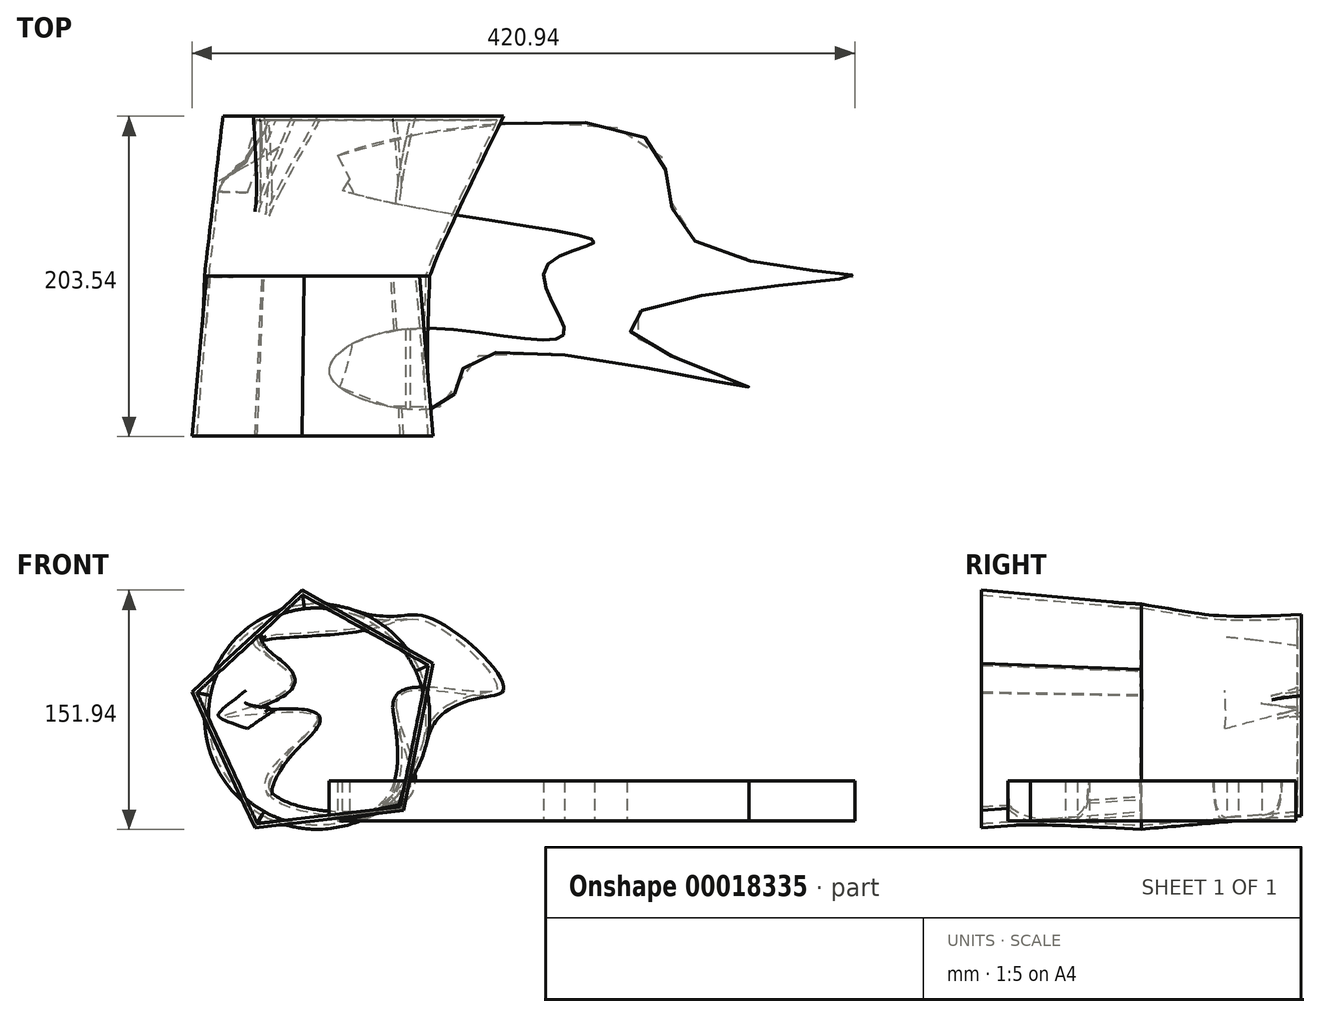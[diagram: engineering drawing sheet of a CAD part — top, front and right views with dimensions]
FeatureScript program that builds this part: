
annotation { "Feature Type Name" : "Feature", "Feature Type Description" : "" }
export const myFeature = defineFeature(function(context is Context, id is Id, definition is map)
    precondition{}
    {
        {
            var Q0;
            Q0=qCreatedBy(makeId("Front.planeOp"),FACE);
            var sketch = newSketch(context, id + "F0", { "sketchPlane" : qUnion([Q0])});
            skFitSpline(sketch, "E0", {"points": [v(0, 0) * mm, v(-33.29, -44.54) * mm, v(59.25, -50.49) * mm, v(52.28, 13.37) * mm, v(117.29, 15.44) * mm, v(73.43, 62.05) * mm, v(28.41, 56.64) * mm, v(-40.52, 46.45) * mm, v(-15.95, 21.27) * mm, v(-59.81, 0) * mm, v(0, 0) * mm]});
            skSolve(sketch);
        }
        {
            var Q0;
            Q0=makeQuery(id+"F0.imprint","IMPRINT",FACE,{"disambiguationData":[TD([[makeQuery(id+"F0.imprint","IMPRINT",EDGE,{"derivedFrom":sQuery(id+"F0.wireOp",EDGE,"E0")}),1.0]])]});
            cPlane(context, id + "F1", {"entities" : qUnion([Q0]), "cplaneType" : CPlaneType.OFFSET, "offset" : 101.6 * mm, "width" : 152.4 * mm, "height" : 152.4 * mm});
        }
        {
            var Q0;
            Q0=qCreatedBy(id+"F1.planeOp",FACE);
            var sketch = newSketch(context, id + "F2", { "sketchPlane" : qUnion([Q0])});
            skPoint(sketch, "E1.0", {"position": v(0, 0) * mm});
            skCircle(sketch, "E2", {"center": v(0, 0) * mm, "radius": 71.56 * mm});
            skSolve(sketch);
        }
        {
            var Q0;
            Q0=makeQuery(id+"F2.imprint","IMPRINT",FACE,{"disambiguationData":[TD([[makeQuery(id+"F2.imprint","IMPRINT",EDGE,{"derivedFrom":sQuery(id+"F2.wireOp",EDGE,"E2")}),1.0]])]});
            var Q1;
            Q1=makeQuery(id+"F0.imprint","IMPRINT",FACE,{"disambiguationData":[TD([[makeQuery(id+"F0.imprint","IMPRINT",EDGE,{"derivedFrom":sQuery(id+"F0.wireOp",EDGE,"E0")}),1.0]])]});
            loft(context, id + "F3", {"sheetProfilesArray" : [{ "sheetProfileEntities" : qUnion([Q0]) }, { "sheetProfileEntities" : qUnion([Q1]) }]});
        }
        {
            var Q0;
            Q0=makeQuery(id+"F3.opLoft","CAP_FACE",FACE,{"disambiguationData":[OSD([makeQuery(id+"F2.imprint","IMPRINT",FACE,{"disambiguationData":[TD([[makeQuery(id+"F2.imprint","IMPRINT",EDGE,{"derivedFrom":sQuery(id+"F2.wireOp",EDGE,"E2")}),1.0]])]})])],"isStart":true});
            cPlane(context, id + "F4", {"entities" : qUnion([Q0]), "cplaneType" : CPlaneType.OFFSET, "offset" : 101.6 * mm, "width" : 152.4 * mm, "height" : 152.4 * mm});
        }
        {
            var Q0;
            Q0=qCreatedBy(id+"F4.planeOp",FACE);
            var sketch = newSketch(context, id + "F5", { "sketchPlane" : qUnion([Q0])});
            skPoint(sketch, "E3.0", {"position": v(0, 0) * mm});
            skCircle(sketch, "E4.cCircle", {"center": v(0, 0) * mm, "radius": 65.48 * mm, "construction": true});
            skLineSegment(sketch, "E4.0", {"start": v(73.5, 33.9) * mm, "end": v(54.95, -59.43) * mm});
            skLineSegment(sketch, "E4.1", {"start": v(54.95, -59.43) * mm, "end": v(-39.54, -70.63) * mm});
            skLineSegment(sketch, "E4.2", {"start": v(-39.54, -70.63) * mm, "end": v(-79.39, 15.78) * mm});
            skLineSegment(sketch, "E4.3", {"start": v(-79.39, 15.78) * mm, "end": v(-9.53, 80.38) * mm});
            skLineSegment(sketch, "E4.4", {"start": v(-9.53, 80.38) * mm, "end": v(73.5, 33.9) * mm});
            skPoint(sketch, "E4.0.midPoint", {"position": v(64.22, -12.76) * mm});
            skSolve(sketch);
        }
        {
            var Q1;
            Q1=makeQuery(id+"F5.imprint","IMPRINT",FACE,{"disambiguationData":[TD([[makeQuery(id+"F5.imprint","IMPRINT",EDGE,{"derivedFrom":sQuery(id+"F5.wireOp",EDGE,"E4.0")}),-1.0]])]});
            var Q2;
            Q2=makeQuery(id+"F3.opLoft","CAP_FACE",FACE,{"disambiguationData":[OSD([makeQuery(id+"F2.imprint","IMPRINT",FACE,{"disambiguationData":[TD([[makeQuery(id+"F2.imprint","IMPRINT",EDGE,{"derivedFrom":sQuery(id+"F2.wireOp",EDGE,"E2")}),1.0]])]})])],"isStart":true});
            loft(context, id + "F6", {"operationType" : NewBodyOperationType.ADD, "sheetProfilesArray" : [{ "sheetProfileEntities" : qUnion([Q1]) }, { "sheetProfileEntities" : qUnion([Q2]) }]});
        }
        {
            var Q0;
            Q0=makeQuery(id+"F6.opLoft","CAP_FACE",FACE,{"disambiguationData":[OSD([makeQuery(id+"F5.imprint","IMPRINT",FACE,{"disambiguationData":[TD([[makeQuery(id+"F5.imprint","IMPRINT",EDGE,{"derivedFrom":sQuery(id+"F5.wireOp",EDGE,"E4.0")}),-1.0]])]})])],"isStart":true});
            shell(context, id + "F7", {"entities" : qUnion([Q0]), "thickness" : 2.54 * mm});
        }
        {
            var Q0;
            Q0=qCreatedBy(makeId("Top.planeOp"),FACE);
            cPlane(context, id + "F8", {"entities" : qUnion([Q0]), "cplaneType" : CPlaneType.OFFSET, "offset" : 66.04 * mm, "oppositeDirection" : true, "width" : 152.4 * mm, "height" : 152.4 * mm});
        }
        {
            var Q0;
            Q0=qCreatedBy(id+"F8.planeOp",FACE);
            var sketch = newSketch(context, id + "F9", { "sketchPlane" : qUnion([Q0])});
            skCircle(sketch, "E5.cCircle", {"center": v(0, -38.76) * mm, "radius": 17.86 * mm, "construction": true});
            skLineSegment(sketch, "E5.0", {"start": v(20.59, -40) * mm, "end": v(9.23, -57.2) * mm});
            skLineSegment(sketch, "E5.1", {"start": v(9.23, -57.2) * mm, "end": v(-11.36, -55.97) * mm});
            skLineSegment(sketch, "E5.2", {"start": v(-11.36, -55.97) * mm, "end": v(-20.59, -37.53) * mm});
            skLineSegment(sketch, "E5.3", {"start": v(-20.59, -37.53) * mm, "end": v(-9.23, -20.31) * mm});
            skLineSegment(sketch, "E5.4", {"start": v(-9.23, -20.31) * mm, "end": v(11.36, -21.54) * mm});
            skLineSegment(sketch, "E5.5", {"start": v(11.36, -21.54) * mm, "end": v(20.59, -40) * mm});
            skPoint(sketch, "E5.0.midPoint", {"position": v(14.9, -48.6) * mm});
            skFitSpline(sketch, "E6", {"points": [v(0, -37.53) * mm, v(206.59, -12.78) * mm, v(235.94, -76.39) * mm, v(341.16, -101.97) * mm, v(196.84, -131.39) * mm, v(274.07, -171.74) * mm, v(101.25, -152.94) * mm, v(82.33, -182.63) * mm, v(9.23, -167.02) * mm, v(54.44, -135.29) * mm, v(156.92, -137.9) * mm, v(145.02, -95.97) * mm, v(175.93, -79.2) * mm, v(0, -37.53) * mm]});
            skSolve(sketch);
        }
        {
            var Q0;
            {var subQ1=sQuery(id+"F9.wireOp",EDGE,"E5.5");var subQ3=sQuery(id+"F9.wireOp",EDGE,"E5.0");var subQ5=makeQuery(id+"F9.imprint","INTERSECT",VERTEX,{"derivedFrom":[subQ3,subQ1]});Q0=makeQuery(id+"F9.imprint","IMPRINT",FACE,{"disambiguationData":[TD([[makeQuery(id+"F9.imprint","IMPRINT",EDGE,{"disambiguationData":[TD([[subQ5,-1.0]])],"derivedFrom":subQ3}),1.0]])]});}
            extrude(context, id + "F10", {"entities" : qUnion([Q0]), "operationType" : NewBodyOperationType.ADD, "depth" : 25.4 * mm});
        }
    });
